# Revit family: Sanitary_Showers_hansgrohe_26963XXX-Vernis-Blend-Showerpipe-200-1jet-with-thermostat-160cc-Varia-Schweden
name_source: partatom
category: Plumbing Fixtures
revit_build: Autodesk Revit 2018 (Build: 20190510_1515(x64)
units: mm (PartAtom-declared; Revit-internal decimal feet)

## family parameters
Always vertical = No
Cut with Voids When Loaded = No
OmniClass Number = 23.31.17.00
OmniClass Title = Showers
Part Type = Normal
Room Calculation Point = No
Round Connector Dimension = Use Diameter
Shared = No
Work Plane-Based = Yes

## types (1)
- 000 Chrome
    Always visible = Yes
    BIMobject category = Showers
    Cold Water Inlet Description = Cold Water Inlet 15DN
    Cold Water Inlet Diameter = 12.7 mm  [stored 0.0416667 ft]
    Default Elevation = 1219.2 mm  [stored 4 ft]
    Description = Vernis Blend Showerpipe 200 1jet with thermostat 160cc Varia Schweden
    Design country = Germany
    Edition number = 1
    Hot Water Inlet Description = Hot Water Inlet 15DN
    Hot Water Inlet Diameter = 12.7 mm  [stored 0.0416667 ft]
    IFC Classification = Sanitary Terminal
    Main Material = Hansgrohe - Metal - 000 Chrome
    Manufacturer = Hansgrohe
    Manufacturer country = Germany
    Manufacturer name = hansgrohe
    Model = 26963XXX Vernis Blend Showerpipe 200 1jet with thermostat 160cc Varia Schweden
    OmniClass Code = 23-31 17 00
    OmniClass Description = Showers
    Product Guid = ab45be84-51c1-440c-a31f-95f51c290e1f
    Product SKU = 26963XXX
    Product data url = https://bimobject.com
    Product family = Vernis Blend
    Product group = Showerpipes with thermostat
    Product name = 26963XXX Vernis Blend Showerpipe 200 1jet with thermostat 160cc Varia Schweden
    Product url = https://www.hansgrohe.com
    QR code = https://bimobject.com
    URL = https://www.hansgrohe.com
    Weight Net (Kg) = 4,9

note: [stored X ft] marks values corroborated as IEEE doubles in the binary element streams (Revit-internal decimal feet)

## geometry (parser evidence)
native form markers: Blend x3, Sweep x2
no freeform markers — native parametric forms only
